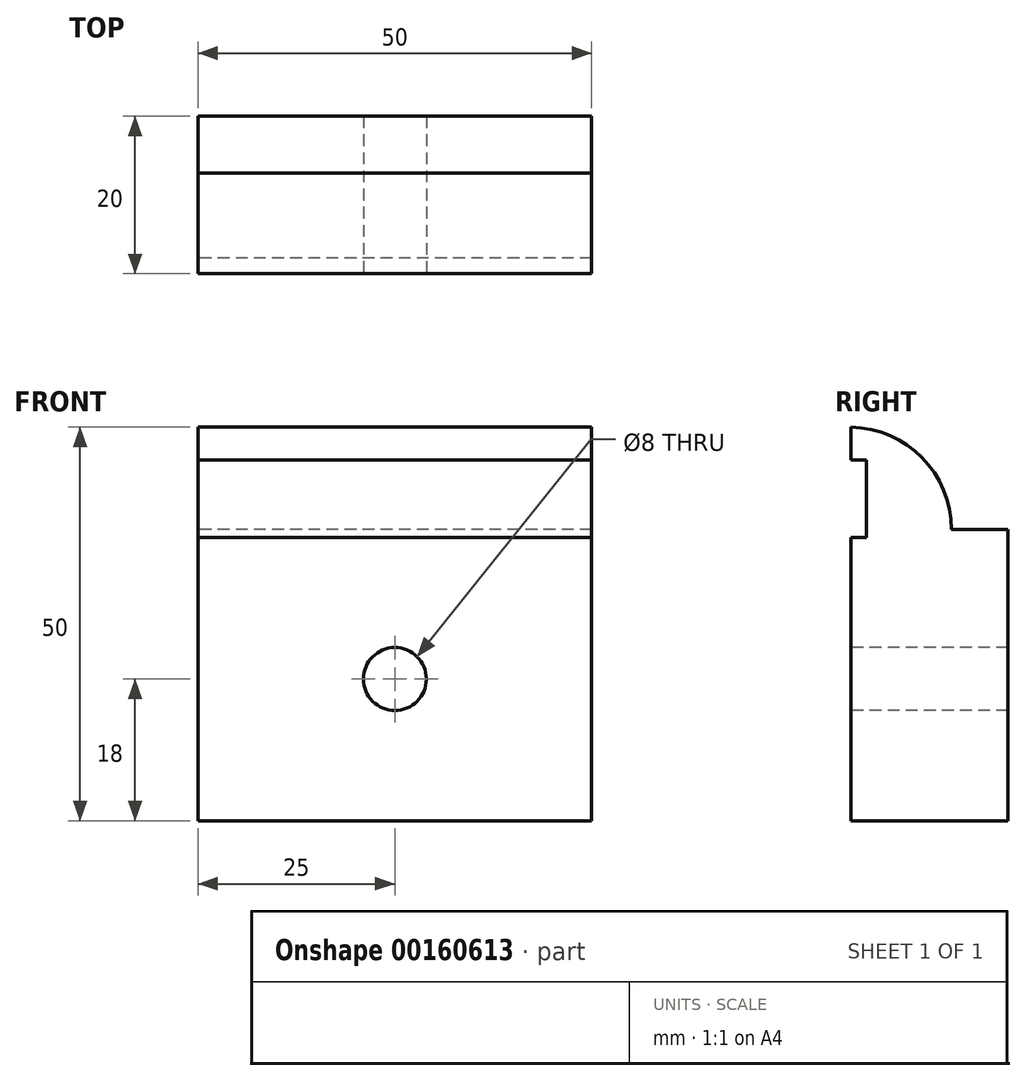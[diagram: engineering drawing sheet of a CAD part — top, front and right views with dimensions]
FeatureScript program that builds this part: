
annotation { "Feature Type Name" : "Feature", "Feature Type Description" : "" }
export const myFeature = defineFeature(function(context is Context, id is Id, definition is map)
    precondition{}
    {
        {
            var Q0;
            Q0=qCreatedBy(makeId("Right.planeOp"),FACE);
            var sketch = newSketch(context, id + "F0", { "sketchPlane" : qUnion([Q0])});
            skLineSegment(sketch, "E0.bottom", {"start": v(-10, 25) * mm, "end": v(-10.2, 25) * mm});
            skLineSegment(sketch, "E0.top", {"start": v(10, -25) * mm, "end": v(-10, -25) * mm});
            skLineSegment(sketch, "E0.left", {"start": v(10, 12) * mm, "end": v(10, -25) * mm});
            skLineSegment(sketch, "E0.right", {"start": v(-10, 25) * mm, "end": v(-10, 20.8) * mm});
            skPoint(sketch, "E0.middle", {"position": v(0, 0) * mm});
            skLineSegment(sketch, "E1.top", {"start": v(10, 12) * mm, "end": v(2.8, 12) * mm});
            skLineSegment(sketch, "E1.right", {"start": v(2.8, 12) * mm, "end": v(2.8, 12) * mm});
            skLineSegment(sketch, "E2", {"start": v(-10, 20.8) * mm, "end": v(-8, 20.8) * mm});
            skLineSegment(sketch, "E3", {"start": v(-8, 20.8) * mm, "end": v(-8, 11) * mm});
            skLineSegment(sketch, "E4", {"start": v(-8, 11) * mm, "end": v(-10, 11) * mm});
            skLineSegment(sketch, "E5.trimOffspring", {"start": v(-10, 11) * mm, "end": v(-10, -25) * mm});
            skPoint(sketch, "E6.visualSharp", {"position": v(2.8, 25) * mm});
            skArc(sketch, "E6.filletArc", {"start": v(2.8, 12) * mm, "mid": v(-1, 21.2) * mm, "end": v(-10.2, 25) * mm});
            skSolve(sketch);
        }
        {
            var Q0;
            Q0=makeQuery(id+"F0.imprint","IMPRINT",FACE,{"disambiguationData":[TD([[makeQuery(id+"F0.imprint","IMPRINT",EDGE,{"derivedFrom":sQuery(id+"F0.wireOp",EDGE,"E0.top")}),-1.0]])]});
            extrude(context, id + "F1", {"entities" : qUnion([Q0]), "depth" : 50 * mm});
        }
        {
            var Q0;
            Q0=makeQuery(id+"F1.opExtrude","SWEPT_FACE",FACE,{"disambiguationData":[OSD([sQuery(id+"F0.wireOp",EDGE,"E5.trimOffspring")])]});
            var sketch = newSketch(context, id + "F2", { "sketchPlane" : qUnion([Q0])});
            skCircle(sketch, "E7", {"center": v(25, -7) * mm, "radius": 4 * mm});
            skSolve(sketch);
        }
        {
            var Q0;
            Q0=makeQuery(id+"F2.imprint","IMPRINT",FACE,{"disambiguationData":[TD([[makeQuery(id+"F2.imprint","IMPRINT",EDGE,{"derivedFrom":sQuery(id+"F2.wireOp",EDGE,"E7")}),1.0]])]});
            extrude(context, id + "F3", {"entities" : qUnion([Q0]), "operationType" : NewBodyOperationType.REMOVE, "oppositeDirection" : true, "depth" : 50 * mm});
        }
    });
